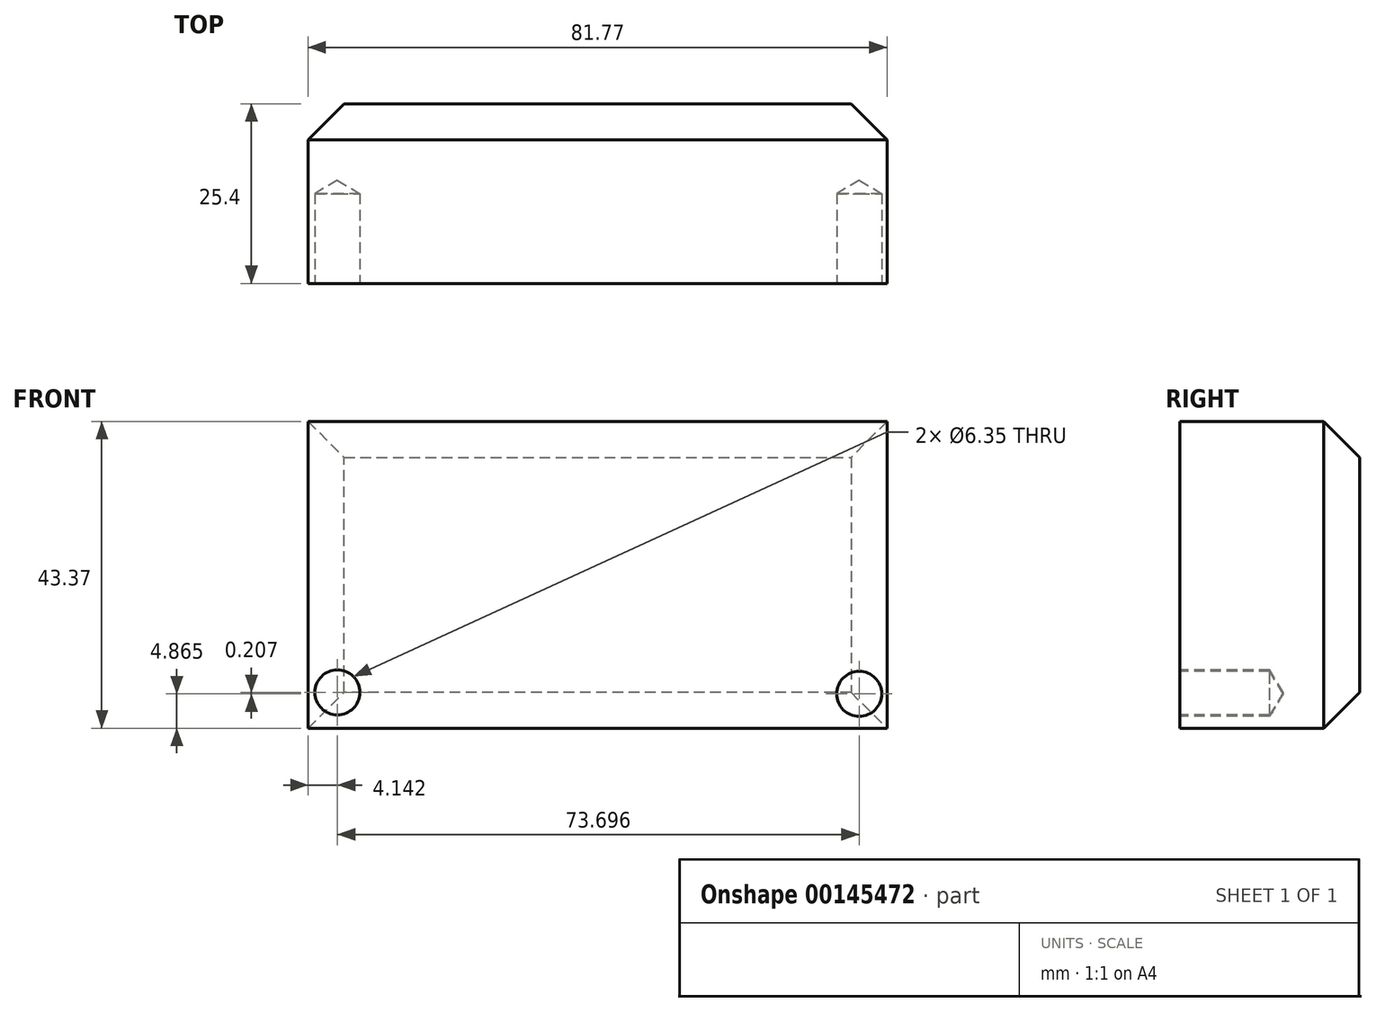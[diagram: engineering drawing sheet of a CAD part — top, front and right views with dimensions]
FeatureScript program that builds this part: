
annotation { "Feature Type Name" : "Feature", "Feature Type Description" : "" }
export const myFeature = defineFeature(function(context is Context, id is Id, definition is map)
    precondition{}
    {
        {
            var Q0;
            Q0=qCreatedBy(makeId("Front.planeOp"),FACE);
            var sketch = newSketch(context, id + "F0", { "sketchPlane" : qUnion([Q0])});
            skLineSegment(sketch, "E0", {"start": v(-40.99, 0) * mm, "end": v(40.78, 0) * mm});
            skLineSegment(sketch, "E1", {"start": v(40.78, 0) * mm, "end": v(40.78, 43.37) * mm});
            skLineSegment(sketch, "E2", {"start": v(40.78, 43.37) * mm, "end": v(-40.99, 43.37) * mm});
            skLineSegment(sketch, "E3", {"start": v(-40.99, 0) * mm, "end": v(-40.99, 43.37) * mm});
            skSolve(sketch);
        }
        {
            var Q0;
            Q0=makeQuery(id+"F0.imprint","IMPRINT",FACE,{"disambiguationData":[TD([[makeQuery(id+"F0.imprint","IMPRINT",EDGE,{"derivedFrom":sQuery(id+"F0.wireOp",EDGE,"E0")}),1.0]])]});
            extrude(context, id + "F1", {"entities" : qUnion([Q0]), "oppositeDirection" : true, "depth" : 25.4 * mm});
        }
        {
            var Q0;
            Q0=qCreatedBy(makeId("Front.planeOp"),FACE);
            var sketch = newSketch(context, id + "F2", { "sketchPlane" : qUnion([Q0])});
            skCircle(sketch, "E4", {"center": v(-36.85, 5.07) * mm, "radius": 3.87 * mm});
            skCircle(sketch, "E5", {"center": v(36.85, 4.86) * mm, "radius": 3.95 * mm});
            skLineSegment(sketch, "E6", {"start": v(-40.69, 10.03) * mm, "end": v(40.99, 10.03) * mm});
            skLineSegment(sketch, "E7", {"start": v(-25.25, 7.49) * mm, "end": v(-25.25, 0) * mm});
            skLineSegment(sketch, "E8", {"start": v(-25.25, 7.49) * mm, "end": v(26.14, 7.49) * mm});
            skLineSegment(sketch, "E9", {"start": v(26.14, 7.49) * mm, "end": v(26.14, 0) * mm});
            skLineSegment(sketch, "E10", {"start": v(26.14, 0) * mm, "end": v(-25.25, 0) * mm});
            skSolve(sketch);
        }
        {
            var Q0;
            Q0=sQuery(id+"F2.wireOp",VERTEX,"E5.center");
            var Q1;
            Q1=sQuery(id+"F2.wireOp",VERTEX,"E4.center");
            var Q2;
            Q2=makeQuery(id+"F1.opExtrude","SWEPT_BODY",BODY,{"disambiguationData":[OSD([sQuery(id+"F0.wireOp",EDGE,"E0"),sQuery(id+"F0.wireOp",EDGE,"E1"),sQuery(id+"F0.wireOp",EDGE,"E2"),sQuery(id+"F0.wireOp",EDGE,"E3")])]});
            hole(context, id + "F3", {"style" : HoleStyle.SIMPLE, "endStyle" : HoleEndStyle.BLIND, "holeDiameter" : 6.35 * mm, "holeDepth" : 12.7 * mm, "locations" : qUnion([Q0, Q1]), "scope" : qUnion([Q2])});
        }
        {
            var Q0;
            Q0=sQuery(id+"F2.wireOp",EDGE,"E6");
            extrude(context, id + "F4", {"bodyType" : ToolBodyType.SURFACE, "surfaceEntities" : qUnion([Q0]), "oppositeDirection" : true, "depth" : 25.4 * mm});
        }
        {
            var Q0;
            Q0=makeQuery(id+"F1.opExtrude","CAP_FACE",FACE,{"disambiguationData":[OSD([sQuery(id+"F0.wireOp",EDGE,"E0"),sQuery(id+"F0.wireOp",EDGE,"E1"),sQuery(id+"F0.wireOp",EDGE,"E2"),sQuery(id+"F0.wireOp",EDGE,"E3")])],"isStart":false});
            chamfer(context, id + "F5", {"entities" : qUnion([Q0]), "width" : 5.08 * mm, "tangentPropagation" : true});
        }
    });
